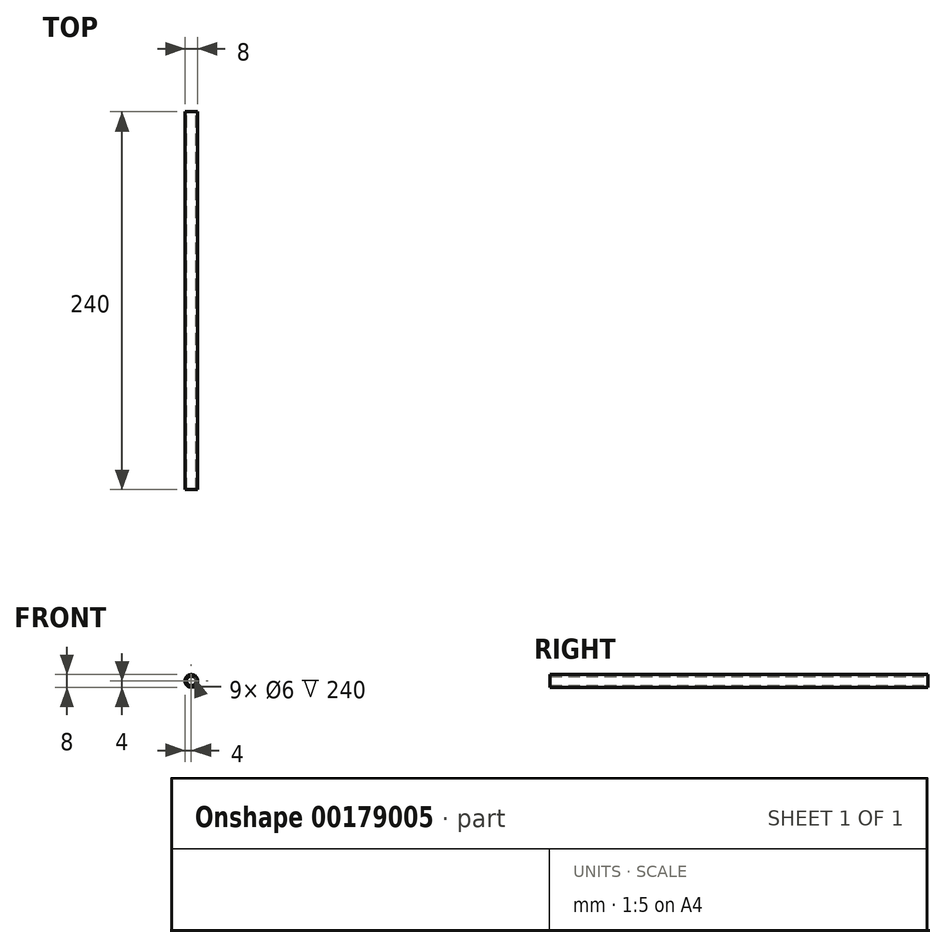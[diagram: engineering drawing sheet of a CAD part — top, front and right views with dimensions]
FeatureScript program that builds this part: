
annotation { "Feature Type Name" : "Feature", "Feature Type Description" : "" }
export const myFeature = defineFeature(function(context is Context, id is Id, definition is map)
    precondition{}
    {
        {
            var Q0;
            Q0=qCreatedBy(makeId("Front.planeOp"),FACE);
            var sketch = newSketch(context, id + "F0", { "sketchPlane" : qUnion([Q0])});
            skCircle(sketch, "E0", {"center": v(0, 0) * mm, "radius": 4 * mm});
            skCircle(sketch, "E1", {"center": v(0, 0) * mm, "radius": 3 * mm});
            skSolve(sketch);
        }
        {
            var Q0;
            Q0 = qSketchRegion(id + "F0", true);
            extrude(context, id + "F1", {"entities" : qUnion([Q0]), "depth" : 240 * mm});
        }
    });
